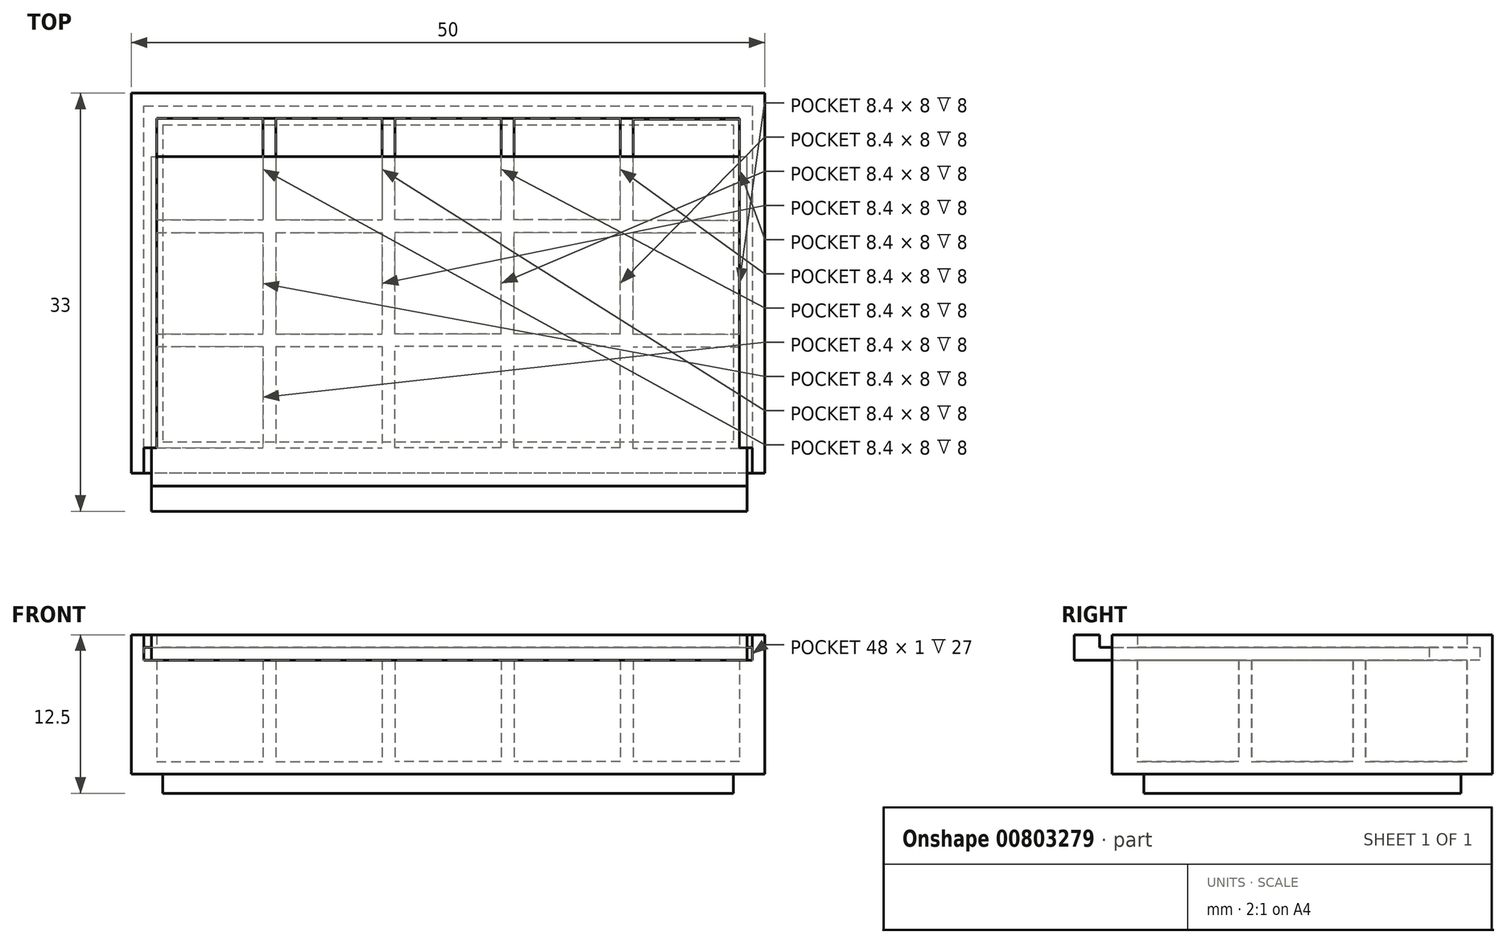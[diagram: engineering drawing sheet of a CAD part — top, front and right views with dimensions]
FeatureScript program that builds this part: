
annotation { "Feature Type Name" : "Feature", "Feature Type Description" : "" }
export const myFeature = defineFeature(function(context is Context, id is Id, definition is map)
    precondition{}
    {
        {
            var Q0;
            Q0=qCreatedBy(makeId("Top.planeOp"),FACE);
            var sketch = newSketch(context, id + "F0", { "sketchPlane" : qUnion([Q0])});
            skLineSegment(sketch, "E0.bottom", {"start": v(25, -15) * mm, "end": v(-25, -15) * mm});
            skLineSegment(sketch, "E0.top", {"start": v(25, 15) * mm, "end": v(-25, 15) * mm});
            skLineSegment(sketch, "E0.left", {"start": v(25, -15) * mm, "end": v(25, 15) * mm});
            skLineSegment(sketch, "E0.right", {"start": v(-25, -15) * mm, "end": v(-25, 15) * mm});
            skLineSegment(sketch, "E1.bottom", {"start": v(-23, 13) * mm, "end": v(-14.6, 13) * mm});
            skLineSegment(sketch, "E1.top", {"start": v(-23, 5) * mm, "end": v(-14.6, 5) * mm});
            skLineSegment(sketch, "E1.left", {"start": v(-23, 13) * mm, "end": v(-23, 5) * mm});
            skLineSegment(sketch, "E1.right", {"start": v(-14.6, 13) * mm, "end": v(-14.6, 5) * mm});
            skLineSegment(sketch, "E2", {"start": v(-23, 13) * mm, "end": v(25, 13) * mm, "construction": true});
            skLineSegment(sketch, "E3.bottom", {"start": v(-13.6, 13) * mm, "end": v(-5.2, 13) * mm});
            skLineSegment(sketch, "E3.top", {"start": v(-13.6, 5) * mm, "end": v(-5.2, 5) * mm});
            skLineSegment(sketch, "E3.left", {"start": v(-13.6, 13) * mm, "end": v(-13.6, 5) * mm});
            skLineSegment(sketch, "E3.right", {"start": v(-5.2, 13) * mm, "end": v(-5.2, 5) * mm});
            skLineSegment(sketch, "E4.bottom", {"start": v(-23, 4) * mm, "end": v(-14.6, 4) * mm});
            skLineSegment(sketch, "E4.top", {"start": v(-23, -4) * mm, "end": v(-14.6, -4) * mm});
            skLineSegment(sketch, "E4.left", {"start": v(-23, 4) * mm, "end": v(-23, -4) * mm});
            skLineSegment(sketch, "E4.right", {"start": v(-14.6, 4) * mm, "end": v(-14.6, -4) * mm});
            skLineSegment(sketch, "E5.bottom", {"start": v(-23, -5) * mm, "end": v(-14.6, -5) * mm});
            skLineSegment(sketch, "E5.top", {"start": v(-23, -13) * mm, "end": v(-14.6, -13) * mm});
            skLineSegment(sketch, "E5.left", {"start": v(-23, -5) * mm, "end": v(-23, -13) * mm});
            skLineSegment(sketch, "E5.right", {"start": v(-14.6, -5) * mm, "end": v(-14.6, -13) * mm});
            skLineSegment(sketch, "E6.bottom", {"start": v(4.2, 5) * mm, "end": v(-4.2, 5) * mm});
            skLineSegment(sketch, "E6.top", {"start": v(4.2, 13) * mm, "end": v(-4.2, 13) * mm});
            skLineSegment(sketch, "E6.left", {"start": v(4.2, 5) * mm, "end": v(4.2, 13) * mm});
            skLineSegment(sketch, "E6.right", {"start": v(-4.2, 5) * mm, "end": v(-4.2, 13) * mm});
            skLineSegment(sketch, "E7.bottom", {"start": v(13.6, 5) * mm, "end": v(5.2, 5) * mm});
            skLineSegment(sketch, "E7.top", {"start": v(13.6, 13) * mm, "end": v(5.2, 13) * mm});
            skLineSegment(sketch, "E7.left", {"start": v(13.6, 5) * mm, "end": v(13.6, 13) * mm});
            skLineSegment(sketch, "E7.right", {"start": v(5.2, 5) * mm, "end": v(5.2, 13) * mm});
            skLineSegment(sketch, "E8.bottom", {"start": v(23, 4.96) * mm, "end": v(14.6, 4.96) * mm});
            skLineSegment(sketch, "E8.top", {"start": v(23, 12.96) * mm, "end": v(14.6, 12.96) * mm});
            skLineSegment(sketch, "E8.left", {"start": v(23, 4.96) * mm, "end": v(23, 12.96) * mm});
            skLineSegment(sketch, "E8.right", {"start": v(14.6, 4.96) * mm, "end": v(14.6, 12.96) * mm});
            skLineSegment(sketch, "E9", {"start": v(-23, -13) * mm, "end": v(25, -13) * mm, "construction": true});
            skLineSegment(sketch, "E10.bottom", {"start": v(-13.6, 4) * mm, "end": v(-5.2, 4) * mm});
            skLineSegment(sketch, "E10.top", {"start": v(-13.6, -4) * mm, "end": v(-5.2, -4) * mm});
            skLineSegment(sketch, "E10.left", {"start": v(-13.6, 4) * mm, "end": v(-13.6, -4) * mm});
            skLineSegment(sketch, "E10.right", {"start": v(-5.2, 4) * mm, "end": v(-5.2, -4) * mm});
            skLineSegment(sketch, "E11.bottom", {"start": v(4.2, -4) * mm, "end": v(-4.2, -4) * mm});
            skLineSegment(sketch, "E11.top", {"start": v(4.2, 4) * mm, "end": v(-4.2, 4) * mm});
            skLineSegment(sketch, "E11.left", {"start": v(4.2, -4) * mm, "end": v(4.2, 4) * mm});
            skLineSegment(sketch, "E11.right", {"start": v(-4.2, -4) * mm, "end": v(-4.2, 4) * mm});
            skLineSegment(sketch, "E12.bottom", {"start": v(13.6, -4) * mm, "end": v(5.2, -4) * mm});
            skLineSegment(sketch, "E12.top", {"start": v(13.6, 4) * mm, "end": v(5.2, 4) * mm});
            skLineSegment(sketch, "E12.left", {"start": v(13.6, -4) * mm, "end": v(13.6, 4) * mm});
            skLineSegment(sketch, "E12.right", {"start": v(5.2, -4) * mm, "end": v(5.2, 4) * mm});
            skLineSegment(sketch, "E13.bottom", {"start": v(23, -4.04) * mm, "end": v(14.6, -4.04) * mm});
            skLineSegment(sketch, "E13.top", {"start": v(23, 3.96) * mm, "end": v(14.6, 3.96) * mm});
            skLineSegment(sketch, "E13.left", {"start": v(23, -4.04) * mm, "end": v(23, 3.96) * mm});
            skLineSegment(sketch, "E13.right", {"start": v(14.6, -4.04) * mm, "end": v(14.6, 3.96) * mm});
            skLineSegment(sketch, "E14.bottom", {"start": v(-13.6, -5) * mm, "end": v(-5.2, -5) * mm});
            skLineSegment(sketch, "E14.top", {"start": v(-13.6, -13) * mm, "end": v(-5.2, -13) * mm});
            skLineSegment(sketch, "E14.left", {"start": v(-13.6, -5) * mm, "end": v(-13.6, -13) * mm});
            skLineSegment(sketch, "E14.right", {"start": v(-5.2, -5) * mm, "end": v(-5.2, -13) * mm});
            skLineSegment(sketch, "E15.bottom", {"start": v(4.2, -13) * mm, "end": v(-4.2, -13) * mm});
            skLineSegment(sketch, "E15.top", {"start": v(4.2, -5) * mm, "end": v(-4.2, -5) * mm});
            skLineSegment(sketch, "E15.left", {"start": v(4.2, -13) * mm, "end": v(4.2, -5) * mm});
            skLineSegment(sketch, "E15.right", {"start": v(-4.2, -13) * mm, "end": v(-4.2, -5) * mm});
            skLineSegment(sketch, "E16.bottom", {"start": v(13.6, -13) * mm, "end": v(5.2, -13) * mm});
            skLineSegment(sketch, "E16.top", {"start": v(13.6, -5) * mm, "end": v(5.2, -5) * mm});
            skLineSegment(sketch, "E16.left", {"start": v(13.6, -13) * mm, "end": v(13.6, -5) * mm});
            skLineSegment(sketch, "E16.right", {"start": v(5.2, -13) * mm, "end": v(5.2, -5) * mm});
            skLineSegment(sketch, "E17.bottom", {"start": v(23, -13.04) * mm, "end": v(14.6, -13.04) * mm});
            skLineSegment(sketch, "E17.top", {"start": v(23, -5.04) * mm, "end": v(14.6, -5.04) * mm});
            skLineSegment(sketch, "E17.left", {"start": v(23, -13.04) * mm, "end": v(23, -5.04) * mm});
            skLineSegment(sketch, "E17.right", {"start": v(14.6, -13.04) * mm, "end": v(14.6, -5.04) * mm});
            skSolve(sketch);
        }
        {
            var Q0;
            Q0=makeQuery(id+"F0.imprint","IMPRINT",FACE,{"disambiguationData":[TD([[makeQuery(id+"F0.imprint","IMPRINT",EDGE,{"derivedFrom":sQuery(id+"F0.wireOp",EDGE,"E0.bottom")}),-1.0]])]});
            extrude(context, id + "F1", {"entities" : qUnion([Q0]), "depth" : 8 * mm, "offsetDistance" : 25 * mm});
        }
        {
            var Q0;
            Q0=makeQuery(id+"F1.opExtrude","CAP_FACE",FACE,{"disambiguationData":[OSD([sQuery(id+"F0.wireOp",EDGE,"E0.bottom"),sQuery(id+"F0.wireOp",EDGE,"E0.top"),sQuery(id+"F0.wireOp",EDGE,"E0.left"),sQuery(id+"F0.wireOp",EDGE,"E0.right"),sQuery(id+"F0.wireOp",EDGE,"E1.bottom"),sQuery(id+"F0.wireOp",EDGE,"E1.top"),sQuery(id+"F0.wireOp",EDGE,"E1.left"),sQuery(id+"F0.wireOp",EDGE,"E1.right"),sQuery(id+"F0.wireOp",EDGE,"E3.bottom"),sQuery(id+"F0.wireOp",EDGE,"E3.top"),sQuery(id+"F0.wireOp",EDGE,"E3.left"),sQuery(id+"F0.wireOp",EDGE,"E3.right"),sQuery(id+"F0.wireOp",EDGE,"E4.bottom"),sQuery(id+"F0.wireOp",EDGE,"E4.top"),sQuery(id+"F0.wireOp",EDGE,"E4.left"),sQuery(id+"F0.wireOp",EDGE,"E4.right"),sQuery(id+"F0.wireOp",EDGE,"E5.bottom"),sQuery(id+"F0.wireOp",EDGE,"E5.top"),sQuery(id+"F0.wireOp",EDGE,"E5.left"),sQuery(id+"F0.wireOp",EDGE,"E5.right"),sQuery(id+"F0.wireOp",EDGE,"E6.bottom"),sQuery(id+"F0.wireOp",EDGE,"E6.top"),sQuery(id+"F0.wireOp",EDGE,"E6.left"),sQuery(id+"F0.wireOp",EDGE,"E6.right"),sQuery(id+"F0.wireOp",EDGE,"E7.bottom"),sQuery(id+"F0.wireOp",EDGE,"E7.top"),sQuery(id+"F0.wireOp",EDGE,"E7.left"),sQuery(id+"F0.wireOp",EDGE,"E7.right"),sQuery(id+"F0.wireOp",EDGE,"E8.bottom"),sQuery(id+"F0.wireOp",EDGE,"E8.top"),sQuery(id+"F0.wireOp",EDGE,"E8.left"),sQuery(id+"F0.wireOp",EDGE,"E8.right"),sQuery(id+"F0.wireOp",EDGE,"E10.bottom"),sQuery(id+"F0.wireOp",EDGE,"E10.top"),sQuery(id+"F0.wireOp",EDGE,"E10.left"),sQuery(id+"F0.wireOp",EDGE,"E10.right"),sQuery(id+"F0.wireOp",EDGE,"E11.bottom"),sQuery(id+"F0.wireOp",EDGE,"E11.top"),sQuery(id+"F0.wireOp",EDGE,"E11.left"),sQuery(id+"F0.wireOp",EDGE,"E11.right"),sQuery(id+"F0.wireOp",EDGE,"E12.bottom"),sQuery(id+"F0.wireOp",EDGE,"E12.top"),sQuery(id+"F0.wireOp",EDGE,"E12.left"),sQuery(id+"F0.wireOp",EDGE,"E12.right"),sQuery(id+"F0.wireOp",EDGE,"E13.bottom"),sQuery(id+"F0.wireOp",EDGE,"E13.top"),sQuery(id+"F0.wireOp",EDGE,"E13.left"),sQuery(id+"F0.wireOp",EDGE,"E13.right"),sQuery(id+"F0.wireOp",EDGE,"E14.bottom"),sQuery(id+"F0.wireOp",EDGE,"E14.top"),sQuery(id+"F0.wireOp",EDGE,"E14.left"),sQuery(id+"F0.wireOp",EDGE,"E14.right"),sQuery(id+"F0.wireOp",EDGE,"E15.bottom"),sQuery(id+"F0.wireOp",EDGE,"E15.top"),sQuery(id+"F0.wireOp",EDGE,"E15.left"),sQuery(id+"F0.wireOp",EDGE,"E15.right"),sQuery(id+"F0.wireOp",EDGE,"E16.bottom"),sQuery(id+"F0.wireOp",EDGE,"E16.top"),sQuery(id+"F0.wireOp",EDGE,"E16.left"),sQuery(id+"F0.wireOp",EDGE,"E16.right"),sQuery(id+"F0.wireOp",EDGE,"E17.bottom"),sQuery(id+"F0.wireOp",EDGE,"E17.top"),sQuery(id+"F0.wireOp",EDGE,"E17.left"),sQuery(id+"F0.wireOp",EDGE,"E17.right")])],"isStart":false});
            var sketch = newSketch(context, id + "F2", { "sketchPlane" : qUnion([Q0])});
            skLineSegment(sketch, "E18", {"start": v(-24, -15) * mm, "end": v(-24, 14) * mm});
            skLineSegment(sketch, "E19", {"start": v(-24, 14) * mm, "end": v(24, 14) * mm});
            skLineSegment(sketch, "E20", {"start": v(24, 14) * mm, "end": v(24, -15) * mm});
            skLineSegment(sketch, "E21", {"start": v(24, -15) * mm, "end": v(25, -15) * mm});
            skLineSegment(sketch, "E22", {"start": v(25, -15) * mm, "end": v(25, 15) * mm});
            skLineSegment(sketch, "E23", {"start": v(25, 15) * mm, "end": v(-25, 15) * mm});
            skLineSegment(sketch, "E24", {"start": v(-25, 15) * mm, "end": v(-25, -15) * mm});
            skLineSegment(sketch, "E25", {"start": v(-25, -15) * mm, "end": v(-24, -15) * mm});
            skSolve(sketch);
        }
        {
            var Q0;
            Q0=makeQuery(id+"F2.imprint","IMPRINT",FACE,{"disambiguationData":[TD([[makeQuery(id+"F2.imprint","IMPRINT",EDGE,{"derivedFrom":sQuery(id+"F2.wireOp",EDGE,"E18")}),1.0]])]});
            extrude(context, id + "F3", {"entities" : qUnion([Q0]), "operationType" : NewBodyOperationType.ADD, "depth" : 1 * mm, "offsetDistance" : 25 * mm});
        }
        {
            var Q0;
            Q0=makeQuery(id+"F3.opExtrude","CAP_FACE",FACE,{"disambiguationData":[OSD([sQuery(id+"F2.wireOp",EDGE,"E18"),sQuery(id+"F2.wireOp",EDGE,"E19"),sQuery(id+"F2.wireOp",EDGE,"E20"),sQuery(id+"F2.wireOp",EDGE,"E21"),sQuery(id+"F2.wireOp",EDGE,"E22"),sQuery(id+"F2.wireOp",EDGE,"E23"),sQuery(id+"F2.wireOp",EDGE,"E24"),sQuery(id+"F2.wireOp",EDGE,"E25")])],"isStart":false});
            var sketch = newSketch(context, id + "F4", { "sketchPlane" : qUnion([Q0])});
            skLineSegment(sketch, "E26", {"start": v(-25, -15) * mm, "end": v(-25, 15) * mm});
            skLineSegment(sketch, "E27", {"start": v(-25, 15) * mm, "end": v(25, 15) * mm});
            skLineSegment(sketch, "E28", {"start": v(25, 15) * mm, "end": v(25, -15) * mm});
            skLineSegment(sketch, "E29", {"start": v(23, 13) * mm, "end": v(-23, 13) * mm});
            skLineSegment(sketch, "E30", {"start": v(-23, 13) * mm, "end": v(-23, -13) * mm});
            skLineSegment(sketch, "E31", {"start": v(-25, -15) * mm, "end": v(-24, -15) * mm});
            skLineSegment(sketch, "E32", {"start": v(-24, -15) * mm, "end": v(-24, -13) * mm});
            skLineSegment(sketch, "E33", {"start": v(-24, -13) * mm, "end": v(-23, -13) * mm});
            skLineSegment(sketch, "E34", {"start": v(23, 13) * mm, "end": v(23, -13) * mm});
            skLineSegment(sketch, "E35", {"start": v(24, -15) * mm, "end": v(24, -15) * mm});
            skLineSegment(sketch, "E36", {"start": v(24, -15) * mm, "end": v(25, -15) * mm});
            skLineSegment(sketch, "E37", {"start": v(23, -13) * mm, "end": v(24, -13) * mm});
            skLineSegment(sketch, "E38", {"start": v(24, -13) * mm, "end": v(24, -15) * mm});
            skSolve(sketch);
        }
        {
            var Q0;
            Q0 = qSketchRegion(id + "F4", true);
            extrude(context, id + "F5", {"entities" : qUnion([Q0]), "operationType" : NewBodyOperationType.ADD, "depth" : 1 * mm, "offsetDistance" : 25 * mm});
        }
        {
            var Q0;
            Q0=makeQuery(id+"F1.opExtrude","CAP_FACE",FACE,{"disambiguationData":[OSD([sQuery(id+"F0.wireOp",EDGE,"E0.bottom"),sQuery(id+"F0.wireOp",EDGE,"E0.top"),sQuery(id+"F0.wireOp",EDGE,"E0.left"),sQuery(id+"F0.wireOp",EDGE,"E0.right"),sQuery(id+"F0.wireOp",EDGE,"E1.bottom"),sQuery(id+"F0.wireOp",EDGE,"E1.top"),sQuery(id+"F0.wireOp",EDGE,"E1.left"),sQuery(id+"F0.wireOp",EDGE,"E1.right"),sQuery(id+"F0.wireOp",EDGE,"E3.bottom"),sQuery(id+"F0.wireOp",EDGE,"E3.top"),sQuery(id+"F0.wireOp",EDGE,"E3.left"),sQuery(id+"F0.wireOp",EDGE,"E3.right"),sQuery(id+"F0.wireOp",EDGE,"E4.bottom"),sQuery(id+"F0.wireOp",EDGE,"E4.top"),sQuery(id+"F0.wireOp",EDGE,"E4.left"),sQuery(id+"F0.wireOp",EDGE,"E4.right"),sQuery(id+"F0.wireOp",EDGE,"E5.bottom"),sQuery(id+"F0.wireOp",EDGE,"E5.top"),sQuery(id+"F0.wireOp",EDGE,"E5.left"),sQuery(id+"F0.wireOp",EDGE,"E5.right"),sQuery(id+"F0.wireOp",EDGE,"E6.bottom"),sQuery(id+"F0.wireOp",EDGE,"E6.top"),sQuery(id+"F0.wireOp",EDGE,"E6.left"),sQuery(id+"F0.wireOp",EDGE,"E6.right"),sQuery(id+"F0.wireOp",EDGE,"E7.bottom"),sQuery(id+"F0.wireOp",EDGE,"E7.top"),sQuery(id+"F0.wireOp",EDGE,"E7.left"),sQuery(id+"F0.wireOp",EDGE,"E7.right"),sQuery(id+"F0.wireOp",EDGE,"E8.bottom"),sQuery(id+"F0.wireOp",EDGE,"E8.top"),sQuery(id+"F0.wireOp",EDGE,"E8.left"),sQuery(id+"F0.wireOp",EDGE,"E8.right"),sQuery(id+"F0.wireOp",EDGE,"E10.bottom"),sQuery(id+"F0.wireOp",EDGE,"E10.top"),sQuery(id+"F0.wireOp",EDGE,"E10.left"),sQuery(id+"F0.wireOp",EDGE,"E10.right"),sQuery(id+"F0.wireOp",EDGE,"E11.bottom"),sQuery(id+"F0.wireOp",EDGE,"E11.top"),sQuery(id+"F0.wireOp",EDGE,"E11.left"),sQuery(id+"F0.wireOp",EDGE,"E11.right"),sQuery(id+"F0.wireOp",EDGE,"E12.bottom"),sQuery(id+"F0.wireOp",EDGE,"E12.top"),sQuery(id+"F0.wireOp",EDGE,"E12.left"),sQuery(id+"F0.wireOp",EDGE,"E12.right"),sQuery(id+"F0.wireOp",EDGE,"E13.bottom"),sQuery(id+"F0.wireOp",EDGE,"E13.top"),sQuery(id+"F0.wireOp",EDGE,"E13.left"),sQuery(id+"F0.wireOp",EDGE,"E13.right"),sQuery(id+"F0.wireOp",EDGE,"E14.bottom"),sQuery(id+"F0.wireOp",EDGE,"E14.top"),sQuery(id+"F0.wireOp",EDGE,"E14.left"),sQuery(id+"F0.wireOp",EDGE,"E14.right"),sQuery(id+"F0.wireOp",EDGE,"E15.bottom"),sQuery(id+"F0.wireOp",EDGE,"E15.top"),sQuery(id+"F0.wireOp",EDGE,"E15.left"),sQuery(id+"F0.wireOp",EDGE,"E15.right"),sQuery(id+"F0.wireOp",EDGE,"E16.bottom"),sQuery(id+"F0.wireOp",EDGE,"E16.top"),sQuery(id+"F0.wireOp",EDGE,"E16.left"),sQuery(id+"F0.wireOp",EDGE,"E16.right"),sQuery(id+"F0.wireOp",EDGE,"E17.bottom"),sQuery(id+"F0.wireOp",EDGE,"E17.top"),sQuery(id+"F0.wireOp",EDGE,"E17.left"),sQuery(id+"F0.wireOp",EDGE,"E17.right")])],"isStart":true});
            var sketch = newSketch(context, id + "F6", { "sketchPlane" : qUnion([Q0])});
            skLineSegment(sketch, "E39.bottom", {"start": v(-25, -15) * mm, "end": v(25, -15) * mm});
            skLineSegment(sketch, "E39.top", {"start": v(-25, 15) * mm, "end": v(25, 15) * mm});
            skLineSegment(sketch, "E39.left", {"start": v(-25, -15) * mm, "end": v(-25, 15) * mm});
            skLineSegment(sketch, "E39.right", {"start": v(25, -15) * mm, "end": v(25, 15) * mm});
            skSolve(sketch);
        }
        {
            var Q0;
            Q0 = qSketchRegion(id + "F6", true);
            extrude(context, id + "F7", {"entities" : qUnion([Q0]), "operationType" : NewBodyOperationType.ADD, "depth" : 1 * mm, "offsetDistance" : 25 * mm});
        }
        {
            var Q0;
            Q0=makeQuery(id+"F1.opExtrude","CAP_FACE",FACE,{"disambiguationData":[OSD([sQuery(id+"F0.wireOp",EDGE,"E0.bottom"),sQuery(id+"F0.wireOp",EDGE,"E0.top"),sQuery(id+"F0.wireOp",EDGE,"E0.left"),sQuery(id+"F0.wireOp",EDGE,"E0.right"),sQuery(id+"F0.wireOp",EDGE,"E1.bottom"),sQuery(id+"F0.wireOp",EDGE,"E1.top"),sQuery(id+"F0.wireOp",EDGE,"E1.left"),sQuery(id+"F0.wireOp",EDGE,"E1.right"),sQuery(id+"F0.wireOp",EDGE,"E3.bottom"),sQuery(id+"F0.wireOp",EDGE,"E3.top"),sQuery(id+"F0.wireOp",EDGE,"E3.left"),sQuery(id+"F0.wireOp",EDGE,"E3.right"),sQuery(id+"F0.wireOp",EDGE,"E4.bottom"),sQuery(id+"F0.wireOp",EDGE,"E4.top"),sQuery(id+"F0.wireOp",EDGE,"E4.left"),sQuery(id+"F0.wireOp",EDGE,"E4.right"),sQuery(id+"F0.wireOp",EDGE,"E5.bottom"),sQuery(id+"F0.wireOp",EDGE,"E5.top"),sQuery(id+"F0.wireOp",EDGE,"E5.left"),sQuery(id+"F0.wireOp",EDGE,"E5.right"),sQuery(id+"F0.wireOp",EDGE,"E6.bottom"),sQuery(id+"F0.wireOp",EDGE,"E6.top"),sQuery(id+"F0.wireOp",EDGE,"E6.left"),sQuery(id+"F0.wireOp",EDGE,"E6.right"),sQuery(id+"F0.wireOp",EDGE,"E7.bottom"),sQuery(id+"F0.wireOp",EDGE,"E7.top"),sQuery(id+"F0.wireOp",EDGE,"E7.left"),sQuery(id+"F0.wireOp",EDGE,"E7.right"),sQuery(id+"F0.wireOp",EDGE,"E8.bottom"),sQuery(id+"F0.wireOp",EDGE,"E8.top"),sQuery(id+"F0.wireOp",EDGE,"E8.left"),sQuery(id+"F0.wireOp",EDGE,"E8.right"),sQuery(id+"F0.wireOp",EDGE,"E10.bottom"),sQuery(id+"F0.wireOp",EDGE,"E10.top"),sQuery(id+"F0.wireOp",EDGE,"E10.left"),sQuery(id+"F0.wireOp",EDGE,"E10.right"),sQuery(id+"F0.wireOp",EDGE,"E11.bottom"),sQuery(id+"F0.wireOp",EDGE,"E11.top"),sQuery(id+"F0.wireOp",EDGE,"E11.left"),sQuery(id+"F0.wireOp",EDGE,"E11.right"),sQuery(id+"F0.wireOp",EDGE,"E12.bottom"),sQuery(id+"F0.wireOp",EDGE,"E12.top"),sQuery(id+"F0.wireOp",EDGE,"E12.left"),sQuery(id+"F0.wireOp",EDGE,"E12.right"),sQuery(id+"F0.wireOp",EDGE,"E13.bottom"),sQuery(id+"F0.wireOp",EDGE,"E13.top"),sQuery(id+"F0.wireOp",EDGE,"E13.left"),sQuery(id+"F0.wireOp",EDGE,"E13.right"),sQuery(id+"F0.wireOp",EDGE,"E14.bottom"),sQuery(id+"F0.wireOp",EDGE,"E14.top"),sQuery(id+"F0.wireOp",EDGE,"E14.left"),sQuery(id+"F0.wireOp",EDGE,"E14.right"),sQuery(id+"F0.wireOp",EDGE,"E15.bottom"),sQuery(id+"F0.wireOp",EDGE,"E15.top"),sQuery(id+"F0.wireOp",EDGE,"E15.left"),sQuery(id+"F0.wireOp",EDGE,"E15.right"),sQuery(id+"F0.wireOp",EDGE,"E16.bottom"),sQuery(id+"F0.wireOp",EDGE,"E16.top"),sQuery(id+"F0.wireOp",EDGE,"E16.left"),sQuery(id+"F0.wireOp",EDGE,"E16.right"),sQuery(id+"F0.wireOp",EDGE,"E17.bottom"),sQuery(id+"F0.wireOp",EDGE,"E17.top"),sQuery(id+"F0.wireOp",EDGE,"E17.left"),sQuery(id+"F0.wireOp",EDGE,"E17.right")])],"isStart":false});
            var sketch = newSketch(context, id + "F8", { "sketchPlane" : qUnion([Q0])});
            skLineSegment(sketch, "E40.bottom", {"start": v(-23.4, -18) * mm, "end": v(23.6, -18) * mm});
            skLineSegment(sketch, "E40.top", {"start": v(-23.4, 10) * mm, "end": v(23.6, 10) * mm});
            skLineSegment(sketch, "E40.left", {"start": v(-23.4, -18) * mm, "end": v(-23.4, 10) * mm});
            skLineSegment(sketch, "E40.right", {"start": v(23.6, -18) * mm, "end": v(23.6, 10) * mm});
            skSolve(sketch);
        }
        {
            var Q0;
            Q0=makeQuery(id+"F7.opExtrude","CAP_FACE",FACE,{"disambiguationData":[OSD([sQuery(id+"F6.wireOp",EDGE,"E39.bottom"),sQuery(id+"F6.wireOp",EDGE,"E39.top"),sQuery(id+"F6.wireOp",EDGE,"E39.left"),sQuery(id+"F6.wireOp",EDGE,"E39.right")])],"isStart":false});
            var sketch = newSketch(context, id + "F9", { "sketchPlane" : qUnion([Q0])});
            skLineSegment(sketch, "E41.bottom", {"start": v(-22.5, -12.5) * mm, "end": v(22.5, -12.5) * mm});
            skLineSegment(sketch, "E41.top", {"start": v(-22.5, 12.5) * mm, "end": v(22.5, 12.5) * mm});
            skLineSegment(sketch, "E41.left", {"start": v(-22.5, -12.5) * mm, "end": v(-22.5, 12.5) * mm});
            skLineSegment(sketch, "E41.right", {"start": v(22.5, -12.5) * mm, "end": v(22.5, 12.5) * mm});
            skSolve(sketch);
        }
        {
            var Q0;
            Q0 = qSketchRegion(id + "F9", true);
            extrude(context, id + "F10", {"entities" : qUnion([Q0]), "operationType" : NewBodyOperationType.ADD, "depth" : 1.5 * mm, "offsetDistance" : 25 * mm});
        }
        {
            var Q0;
            Q0 = qSketchRegion(id + "F8", true);
            extrude(context, id + "F11", {"entities" : qUnion([Q0]), "depth" : 1 * mm, "offsetDistance" : 25 * mm});
        }
        {
            var Q0;
            Q0=makeQuery(id+"F11.opExtrude","CAP_FACE",FACE,{"disambiguationData":[OSD([sQuery(id+"F8.wireOp",EDGE,"E40.bottom"),sQuery(id+"F8.wireOp",EDGE,"E40.top"),sQuery(id+"F8.wireOp",EDGE,"E40.left"),sQuery(id+"F8.wireOp",EDGE,"E40.right")])],"isStart":false});
            var sketch = newSketch(context, id + "F12", { "sketchPlane" : qUnion([Q0])});
            skLineSegment(sketch, "E42", {"start": v(-23.4, -18) * mm, "end": v(23.6, -18) * mm});
            skLineSegment(sketch, "E43", {"start": v(23.6, -18) * mm, "end": v(23.6, -16) * mm});
            skLineSegment(sketch, "E44", {"start": v(23.6, -16) * mm, "end": v(-23.4, -16) * mm});
            skLineSegment(sketch, "E45", {"start": v(-23.4, -16) * mm, "end": v(-23.4, -18) * mm});
            skSolve(sketch);
        }
        {
            var Q0;
            Q0 = qSketchRegion(id + "F12", true);
            extrude(context, id + "F13", {"entities" : qUnion([Q0]), "operationType" : NewBodyOperationType.ADD, "depth" : 1 * mm, "offsetDistance" : 25 * mm});
        }
    });
